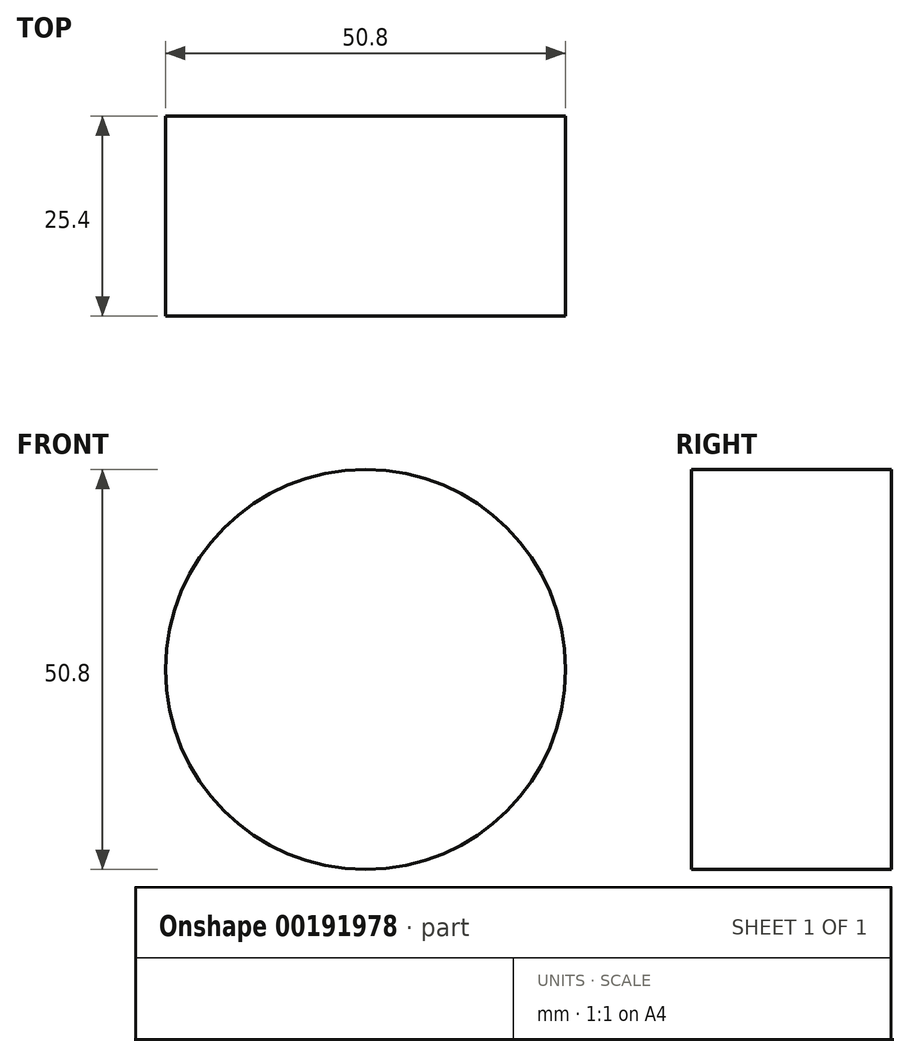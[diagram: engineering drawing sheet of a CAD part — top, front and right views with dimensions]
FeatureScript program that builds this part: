
annotation { "Feature Type Name" : "Feature", "Feature Type Description" : "" }
export const myFeature = defineFeature(function(context is Context, id is Id, definition is map)
    precondition{}
    {
        {
            var Q0;
            Q0=qCreatedBy(makeId("Front.planeOp"),FACE);
            var sketch = newSketch(context, id + "F0", { "sketchPlane" : qUnion([Q0])});
            skCircle(sketch, "E0", {"center": v(0, 0) * mm, "radius": 25.4 * mm});
            skSolve(sketch);
        }
        {
            var Q0;
            Q0 = qSketchRegion(id + "F0", true);
            extrude(context, id + "F1", {"entities" : qUnion([Q0]), "depth" : 25.4 * mm, "symmetric" : true});
        }
    });
